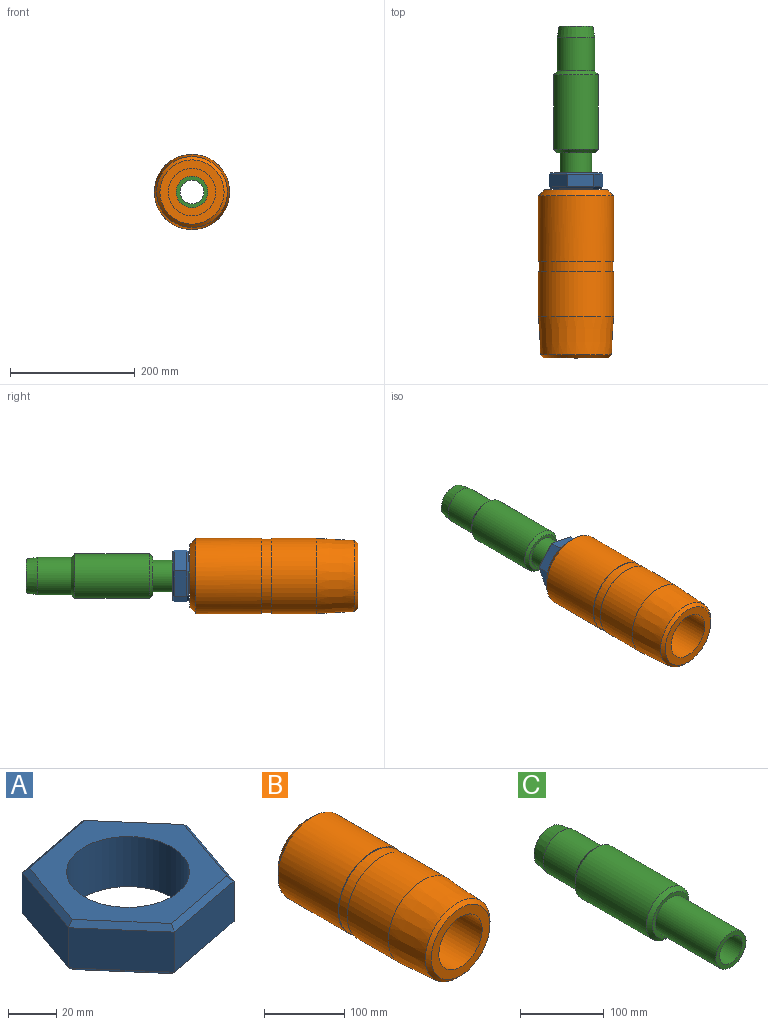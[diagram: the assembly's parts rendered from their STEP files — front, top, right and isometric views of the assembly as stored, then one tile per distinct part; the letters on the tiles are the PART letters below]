
ASSEMBLY  parts=3 mates=2
PART A: 21 faces, bbox 86.4x83.2x25.4 mm
  f0: plane 43.2x20.32mm, normal (-0.19,0.98,0), area 894mm2, adj f1,f5,f13,f19
  f1: plane 41.58x20.32mm, normal (-0.95,0.33,0), area 894mm2, adj f0,f2,f14,f20
  f2: plane 33.24x28.82mm, normal (-0.76,-0.66,0), area 894mm2, adj f1,f3,f12,f18
  f3: plane 43.2x20.32mm, normal (0.19,-0.98,0), area 894mm2, adj f2,f4,f10,f16
  f4: plane 41.58x20.32mm, normal (0.95,-0.33,0), area 894mm2, adj f3,f5,f9,f15
  f5: plane 33.24x28.82mm, normal (0.76,0.66,0), area 894mm2, adj f0,f4,f11,f17
  f6: cylinder r=25.4mm len=50.8mm, axis (0,0,-1), area 4053.7mm2, adj f7,f8
  f7: plane 80.63x77.62mm, normal (0,0,1), area 2353.6mm2, adj f6,f15,f16,f17,f18,f19,f20
  f8: plane 80.63x77.62mm, normal (0,0,-1), area 2353.6mm2, adj f6,f9,f10,f11,f12,f13,f14
  f9: plane 41.58x16.3mm, normal (0.67,-0.23,-0.71), area 152.8mm2, adj f4,f8,f10,f11
  f10: plane 43.2x10.56mm, normal (0.13,-0.69,-0.71), area 152.8mm2, adj f3,f8,f9,f12
  f11: plane 33.79x29.78mm, normal (0.53,0.46,-0.71), area 152.8mm2, adj f5,f8,f9,f13
  f12: plane 33.79x29.78mm, normal (-0.53,-0.46,-0.71), area 152.8mm2, adj f2,f8,f10,f14
  f13: plane 43.2x10.56mm, normal (-0.13,0.69,-0.71), area 152.8mm2, adj f0,f8,f11,f14
  f14: plane 41.58x16.3mm, normal (-0.67,0.23,-0.71), area 152.8mm2, adj f1,f8,f12,f13
  f15: plane 41.58x16.3mm, normal (0.67,-0.23,0.71), area 152.8mm2, adj f4,f7,f16,f17
  f16: plane 43.2x10.56mm, normal (0.13,-0.69,0.71), area 152.8mm2, adj f3,f7,f15,f18
  f17: plane 33.79x29.78mm, normal (0.53,0.46,0.71), area 152.8mm2, adj f5,f7,f15,f19
  f18: plane 33.79x29.78mm, normal (-0.53,-0.46,0.71), area 152.8mm2, adj f2,f7,f16,f20
  f19: plane 43.2x10.56mm, normal (-0.13,0.69,0.71), area 152.8mm2, adj f0,f7,f17,f20
  f20: plane 41.58x16.3mm, normal (-0.67,0.23,0.71), area 152.8mm2, adj f1,f7,f18,f19
PART B: 13 faces, bbox 120.7x269.9x120.7 mm
  f0: plane 101.6x101.6mm, normal (0,1,0), area 6080.5mm2, adj f10,f11
  f1: cylinder r=60.32mm len=120.65mm, axis (0,-1,0), area 40150.2mm2, adj f2,f11
  f2: plane 120.65x120.65mm, normal (0,-1,0), area 381.9mm2, adj f1,f3
  f3: cylinder r=59.31mm len=118.62mm, axis (0,-1,0), area 5860.6mm2, adj f2,f4
  f4: plane 120.65x120.65mm, normal (0,1,0), area 381.9mm2, adj f3,f5
  f5: cylinder r=60.32mm len=120.65mm, axis (0,-1,0), area 27353.2mm2, adj f4,f6
  f6: cone r=60.32mm half-angle=3.2deg, axis (0,1,0), area 22672.4mm2, adj f5,f12
  f7: plane 102.95x102.95mm, normal (0,-1,0), area 3770.3mm2, adj f8,f12
  f8: cylinder r=38.07mm len=161.96mm, axis (0,-1,0), area 38743.5mm2, adj f7,f9
  f9: plane 76.14x76.14mm, normal (0,-1,0), area 2526.7mm2, adj f8,f10
  f10: cylinder r=25.4mm len=107.95mm, axis (0,-1,0), area 17228.1mm2, adj f0,f9
  f11: cone r=60.32mm half-angle=45deg, axis (0,-1,0), area 4702.6mm2, adj f0,f1
  f12: cone r=51.47mm half-angle=46.6deg, axis (0,1,0), area 2512.8mm2, adj f6,f7
PART C: 10 faces, bbox 71.9x304.8x71.9 mm
  f0: plane 61.77x61.77mm, normal (0,-1,0), area 969.5mm2, adj f1,f9
  f1: cylinder r=25.4mm len=101.6mm, axis (0,-1,0), area 16214.6mm2, adj f0,f2
  f2: plane 50.8x50.8mm, normal (0,-1,0), area 886.7mm2, adj f1,f8
  f3: plane 54.25x54.25mm, normal (0,1,0), area 1171.5mm2, adj f4,f8
  f4: cone r=30.16mm half-angle=9.2deg, axis (0,-1,0), area 3410.4mm2, adj f3,f5
  f5: cylinder r=30.16mm len=60.33mm, axis (0,-1,0), area 10130.2mm2, adj f4,f6
  f6: cone r=30.16mm half-angle=45deg, axis (0,-1,0), area 1704.2mm2, adj f5,f7
  f7: cylinder r=35.96mm len=120.16mm, axis (0,-1,0), area 27152.3mm2, adj f6,f9
  f8: cylinder r=19.05mm len=304.8mm, axis (0,1,0), area 36482.9mm2, adj f2,f3
  f9: cone r=30.88mm half-angle=45deg, axis (0,1,0), area 1508.7mm2, adj f0,f7
PLACE A rot(axis=(-1,0,0),90deg) t=(-28.91,-55.62,-150.86)mm
PLACE B t=(-28.91,-183.7,-150.86)mm
PLACE C t=(-28.91,38.46,-150.86)mm
MATE slider B.f1 <-> C.f1  axis (0,1,0) through (-28.91,-57.5,-150.86)mm
MATE slider A.f6 <-> C.f1  axis (0,-1,0) through (-28.91,-55.62,-150.86)mm
